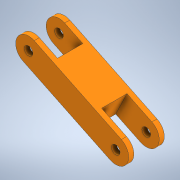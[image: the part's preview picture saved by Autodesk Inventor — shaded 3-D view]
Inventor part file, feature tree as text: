
AUTODESK INVENTOR PART (.ipt)
format: ipt  version: 2021 (Build 250183000, 183)  size: 146,432 bytes
history: native  units: mm
features: extrude x3, sketch x3
ambient origin geometry x8: Origin, YZ Plane, XZ Plane, XY Plane, X Axis, Y Axis, Z Axis, Center Point
bodies: Solid1 (feature_tree)
feature tree (6):
  extrude  "Extrusion1"  Depth=150.0mm
  extrude  "Extrusion2"  Depth=150.0mm
  extrude  "Extrusion3"  Depth=207.0mm TaperAngle=0.0deg
  sketch  "Sketch1"  dims[d0=150.0mm d1=50.0mm]
  sketch  "Sketch2"  dims[d2=150.0mm d3=50.0mm]
  sketch  "Sketch3"  dims[d4=562.0mm d5=207.0mm d6=0.0mm d7=30.0mm d8=207.0mm d9=0.0mm d10=30.0mm d11=207.0mm d12=0.0mm]
